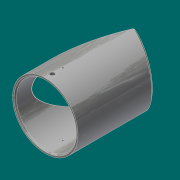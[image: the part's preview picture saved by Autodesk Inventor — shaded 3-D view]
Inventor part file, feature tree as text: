
AUTODESK INVENTOR PART (.ipt)
format: ipt  version: 2017.3 (Build 213257000, 257)  size: 481,280 bytes
history: native  units: in
note: dims shown in document units (in); Inventor stores cm internally (conversion verified against a paired STEP export)
features: other x21, split x9, loft x8, extrude x7, sketch x4, plane x4, hole x2, chamfer x1, pattern_circular x1
ambient origin geometry x8: Origin, YZ Plane, XZ Plane, XY Plane, X Axis, Y Axis, Z Axis, Center Point
bodies: Solid1 (feature_tree)
feature tree (57):
  sketch  "Sketch1"  dims[d0=34.25in d1=37.25in]
  extrude  "Extrusion1"  Depth=37.25in
  sketch  "Sketch2"  dims[d2=50.9606in d3=0.0in d4=22.5deg]
  extrude  "Extrusion2"  TaperAngle=22.5deg  [1 undecoded]
  split  "Split1"
  split  "Split2"
  plane  "Work Plane1"
  plane  "Work Plane2"
  split  "Split3"
  split  "Split4"
  split  "Split5"
  loft  "Loft5"
  loft  "Loft6"
  loft  "Loft7"
  loft  "Loft8"
  loft  "Loft9"
  loft  "Loft10"
  loft  "Loft11"
  plane  "Work Plane3"
  split  "Split6"
  loft  "Loft13"
  chamfer  "Chamfer1"  Angle=90.0deg  [1 undecoded]
  plane  "Work Plane4"
  sketch  "Sketch4"  dims[d5=60.0079in d6=0.0in d7=34.375in]
  hole  "Hole1"  [1 undecoded]
  split  "Split7"
  hole  "Hole2"  [1 undecoded]
  pattern_circular  "Circular Pattern1"  Angle=90.0deg  [1 undecoded]
  sketch  "Sketch5"  dims[d8=0.0in d9=0.0in d10=0.0469in d11=0.0469in d13=1.103in d14=1.103in d15=60.0079in d16=0.0in d18=-1.103in d19=-1.103in d36=0.0in d37=90.0deg d38=0.0in d39=90.0deg d40=0.0in d41=90.0deg d42=0.0in d43=90.0deg d44=0.0in d45=90.0deg d46=0.0in d47=90.0deg d48=0.0in d49=90.0deg d50=0.0in d51=90.0deg d52=0.0in d53=90.0deg d54=0.0in d55=90.0deg d56=0.0in d57=90.0deg d58=0.0in d59=90.0deg d60=0.0in d61=90.0deg d62=0.0in d63=90.0deg d68=0.0in d69=90.0deg d70=0.0in d71=90.0deg d72=0.75in d73=0.125in d74=0.2749in d75=4.0in d76=4.125in d77=2.5625in d78=0.75in d79=0.375in d80=0.25in d81=0.5635in d82=2.0in d83=0.8108in d84=1.0in d85=0.0in d86=6.0in d87=0.891in d88=0.553in d89=0.0246in d90=0.897in d91=0.375in d92=0.25in d93=0.5635in d94=2.0in d95=0.8108in d96=0.7874in d97=360.0deg d99=0.0625in d100=0.0938in d101=75.0deg d102=0.0in d103=0.0in d104=0.0in d105=0.0in]
  split  "Split8"
  split  "Split9"
  other  "Srf1"
  other  "Srf2"
  other  "Edges9"
  other  "Edges10"
  other  "Edges11"
  other  "Edges12"
  other  "Edges13"
  other  "Edges14"
  other  "Edges15"
  other  "Edges16"
  other  "Edges17"
  other  "Edges18"
  other  "Edges19"
  other  "Edges20"
  other  "Edges21"
  other  "Edges22"
  other  "Edges25"
  other  "Edges26"
  other  "Srf3"
  other  "Srf4"
  other  "Srf5"
  extrude  "ExtrusionSrf1"  TaperAngle=0.0deg  [1 undecoded]
  extrude  "ExtrusionSrf2"  TaperAngle=0.0deg  [1 undecoded]
  extrude  "ExtrusionSrf3"  TaperAngle=0.0deg  [1 undecoded]
  extrude  "ExtrusionSrf4"  TaperAngle=0.0deg  [1 undecoded]
  extrude  "ExtrusionSrf5"  TaperAngle=0.0deg  [1 undecoded]
note: 10 required parameter values undecoded (feature->parameter linkage not recoverable at this tier; creation-order binding heuristic only, values carry confidence <= 0.55)
